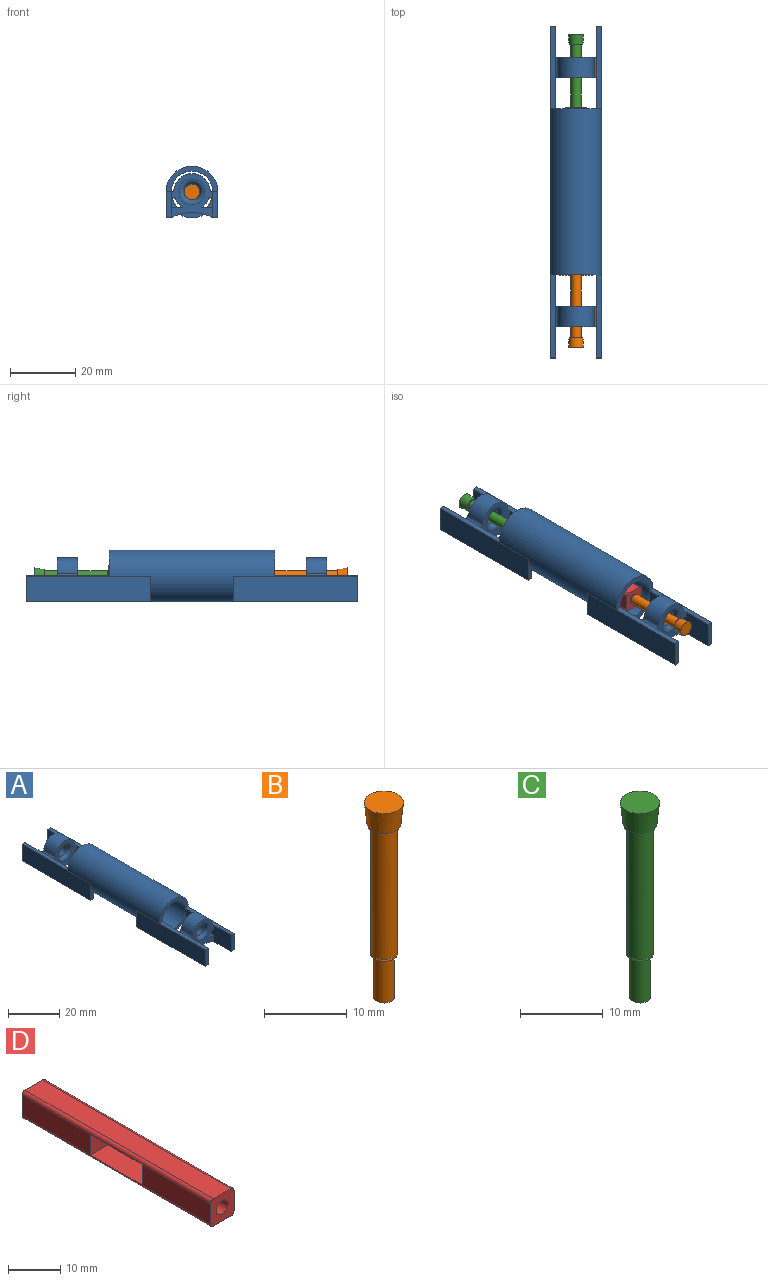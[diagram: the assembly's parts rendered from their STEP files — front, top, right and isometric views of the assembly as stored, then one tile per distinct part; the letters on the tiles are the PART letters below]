
ASSEMBLY  parts=4 mates=3
PART A: 68 faces, bbox 15.9x101.6x15.9 mm
  f0: cylinder r=6.35mm len=9.53mm, axis (0,1,0), area 1.3mm2, adj f2,f30,f31,f50
  f1: cylinder r=6.35mm len=69.85mm, axis (0,1,0), area 2031.9mm2, adj f2,f3,f4,f5,f8,f9,f10,f11
  f2: plane 38.1x7.87mm, normal (1,0,0), area 210.4mm2, adj f0,f1,f9,f15,f16,f22,f31,f45
  f3: plane 38.1x7.87mm, normal (-1,0,0), area 210.4mm2, adj f1,f7,f9,f12,f16,f24,f33,f47
  f4: plane 38.1x7.87mm, normal (1,0,0), area 210.4mm2, adj f1,f11,f16,f20,f21,f23,f27,f39
  f5: plane 38.1x7.87mm, normal (-1,0,0), area 210.4mm2, adj f1,f6,f11,f16,f17,f25,f29,f35
  f6: cylinder r=6.35mm len=9.53mm, axis (0,1,0), area 1.3mm2, adj f5,f28,f29,f41
  f7: cylinder r=6.35mm len=9.53mm, axis (0,1,0), area 1.3mm2, adj f3,f32,f33,f50
  f8: plane 15.87x7.87mm, normal (0,1,0), area 35.4mm2, adj f1,f16,f30,f32
  f9: plane 12.7x7.87mm, normal (0,1,0), area 25.3mm2, adj f1,f2,f3,f16
  f10: plane 15.87x7.87mm, normal (0,-1,0), area 35.4mm2, adj f1,f16,f26,f28
  f11: plane 12.7x7.87mm, normal (0,-1,0), area 25.3mm2, adj f1,f4,f5,f16
  f12: plane 38.1x1.59mm, normal (0,0,-1), area 60.5mm2, adj f3,f13,f24,f33,f53
  f13: plane 38.1x8mm, normal (1,0,0), area 303.3mm2, adj f12,f16,f24,f32,f33
  f14: plane 38.1x7.87mm, normal (-1,0,0), area 299.9mm2, adj f15,f16,f22,f31
  f15: plane 38.1x1.59mm, normal (0,0,-1), area 60.5mm2, adj f2,f14,f22,f31,f52
  f16: cylinder r=7.94mm len=101.6mm, axis (0,1,0), area 2284.2mm2, adj f2,f3,f4,f5,f8,f9,f10,f11
  f17: plane 38.1x1.59mm, normal (0,0,-1), area 60.5mm2, adj f5,f18,f25,f29,f54
  f18: plane 38.1x8mm, normal (1,0,0), area 303.3mm2, adj f16,f17,f25,f28,f29
  f19: plane 38.1x7.87mm, normal (-1,0,0), area 299.9mm2, adj f16,f20,f23,f27
  f20: plane 38.1x1.59mm, normal (0,0,-1), area 60.5mm2, adj f4,f19,f23,f27,f55
  f21: cylinder r=6.35mm len=9.53mm, axis (0,1,0), area 1.3mm2, adj f4,f26,f27,f41
  f22: plane 7.87x1.59mm, normal (0,-1,0), area 7.4mm2, adj f2,f14,f15,f16
  f23: plane 7.87x1.59mm, normal (0,1,0), area 7.4mm2, adj f4,f16,f19,f20
  f24: plane 7.87x1.59mm, normal (0,-1,0), area 7.4mm2, adj f3,f12,f13,f16
  f25: plane 7.87x1.59mm, normal (0,1,0), area 7.4mm2, adj f5,f16,f17,f18
  f26: plane 25.4x1.67mm, normal (0,0,1), area 40.8mm2, adj f1,f10,f16,f21,f27,f41,f42,f67
  f27: plane 8x1.59mm, normal (0,-1,0), area 12.7mm2, adj f4,f16,f19,f20,f21,f26
  f28: plane 25.4x1.67mm, normal (0,0,1), area 40.8mm2, adj f1,f6,f10,f18,f29,f41,f42,f66
  f29: plane 8x1.59mm, normal (0,-1,0), area 12.7mm2, adj f5,f6,f17,f18,f28
  f30: plane 25.4x1.67mm, normal (0,0,1), area 40.8mm2, adj f0,f1,f8,f16,f31,f50,f51,f65
  f31: plane 8x1.59mm, normal (0,1,0), area 12.7mm2, adj f0,f2,f14,f15,f16,f30
  f32: plane 25.4x1.67mm, normal (0,0,1), area 40.8mm2, adj f1,f7,f8,f13,f33,f50,f51,f64
  f33: plane 8x1.59mm, normal (0,1,0), area 12.7mm2, adj f3,f7,f12,f13,f32
  f34: plane 6.35x0.16mm, normal (0,0,-1), area 1mm2, adj f41,f42,f54,f55
  f35: plane 6.35x3.49mm, normal (0,0,1), area 22.1mm2, adj f5,f36,f41,f42
  f36: cylinder r=5.56mm len=6.35mm, axis (0,1,0), area 20.1mm2, adj f35,f41,f42,f62
  f37: cylinder r=5.56mm len=11.03mm, axis (0,1,0), area 102.3mm2, adj f41,f42,f66,f67
  f38: cylinder r=5.56mm len=6.35mm, axis (0,1,0), area 20.1mm2, adj f39,f41,f42,f63
  f39: plane 6.35x3.49mm, normal (0,0,1), area 22.1mm2, adj f4,f38,f41,f42
  f40: cylinder r=2.38mm len=4.76mm, axis (0,1,0), area 47.5mm2, adj f58,f59
  f41: plane 13.56x12.7mm, normal (0,-1,0), area 74.7mm2, adj f4,f5,f6,f21,f26,f28,f34,f35
  f42: plane 13.56x12.7mm, normal (0,1,0), area 74.7mm2, adj f1,f4,f5,f26,f28,f34,f35,f36
  f43: cylinder r=5.56mm len=11.03mm, axis (0,-1,0), area 102.3mm2, adj f50,f51,f64,f65
  f44: cylinder r=5.56mm len=6.35mm, axis (0,-1,0), area 20.1mm2, adj f45,f50,f51,f61
  f45: plane 6.35x3.49mm, normal (0,0,1), area 22.1mm2, adj f2,f44,f50,f51
  f46: plane 6.35x0.16mm, normal (0,0,-1), area 1mm2, adj f50,f51,f52,f53
  f47: plane 6.35x3.49mm, normal (0,0,1), area 22.1mm2, adj f3,f48,f50,f51
  f48: cylinder r=5.56mm len=6.35mm, axis (0,-1,0), area 20.1mm2, adj f47,f50,f51,f60
  f49: cylinder r=2.38mm len=4.76mm, axis (0,-1,0), area 47.5mm2, adj f56,f57
  f50: plane 13.56x12.7mm, normal (0,1,0), area 74.7mm2, adj f0,f2,f3,f7,f30,f32,f43,f44
  f51: plane 13.56x12.7mm, normal (0,-1,0), area 74.7mm2, adj f1,f2,f3,f30,f32,f43,f44,f45
  f52: cylinder r=12.7mm len=6.35mm, axis (0,-1,0), area 41.6mm2, adj f15,f46,f50,f51
  f53: cylinder r=12.7mm len=6.35mm, axis (0,1,0), area 41.6mm2, adj f12,f46,f50,f51
  f54: cylinder r=12.7mm len=6.35mm, axis (0,1,0), area 41.6mm2, adj f17,f34,f41,f42
  f55: cylinder r=12.7mm len=6.35mm, axis (0,-1,0), area 41.6mm2, adj f20,f34,f41,f42
  f56: torus R=3.97mm, axis (0,-1,0), area 46.3mm2, adj f49,f51
  f57: torus R=3.97mm, axis (0,-1,0), area 46.3mm2, adj f49,f50
  f58: torus R=3.97mm, axis (0,-1,0), area 46.3mm2, adj f40,f42
  f59: torus R=3.97mm, axis (0,-1,0), area 46.3mm2, adj f40,f41
  f60: cylinder r=1.59mm len=6.35mm, axis (0,1,0), area 10.9mm2, adj f3,f48,f50,f51
  f61: cylinder r=1.59mm len=6.35mm, axis (0,1,0), area 10.9mm2, adj f2,f44,f50,f51
  f62: cylinder r=1.59mm len=6.35mm, axis (0,-1,0), area 10.9mm2, adj f5,f36,f41,f42
  f63: cylinder r=1.59mm len=6.35mm, axis (0,-1,0), area 10.9mm2, adj f4,f38,f41,f42
  f64: cylinder r=0.76mm len=6.35mm, axis (0,-1,0), area 7mm2, adj f32,f43,f50,f51
  f65: cylinder r=0.76mm len=6.35mm, axis (0,-1,0), area 7mm2, adj f30,f43,f50,f51
  f66: cylinder r=0.76mm len=6.35mm, axis (0,1,0), area 7mm2, adj f28,f37,f41,f42
  f67: cylinder r=0.76mm len=6.35mm, axis (0,1,0), area 7mm2, adj f26,f37,f41,f42
PART B: 8 faces, bbox 4.8x4.8x28.9 mm
  f0: cylinder r=1.27mm len=6.35mm, axis (0,0,-1), area 50.7mm2, adj f1,f2
  f1: plane 2.54x2.54mm, normal (0,0,-1), area 5.1mm2, adj f0
  f2: plane 2.98x2.98mm, normal (0,0,-1), area 1.9mm2, adj f0,f3
  f3: torus R=1.49mm, axis (0,0,1), area 4mm2, adj f2,f4
  f4: cylinder r=1.59mm len=19.08mm, axis (0,0,-1), area 190.3mm2, adj f3,f6
  f5: plane 4.76x4.76mm, normal (0,0,1), area 17.8mm2, adj f7
  f6: plane 4.13x4.13mm, normal (0,0,-1), area 5.5mm2, adj f4,f7
  f7: cone r=2.38mm half-angle=5.7deg, axis (0,0,1), area 44.6mm2, adj f5,f6
PART C: 8 faces, bbox 4.8x4.8x28.9 mm
  f0: cylinder r=1.27mm len=6.35mm, axis (0,0,-1), area 50.7mm2, adj f1,f2
  f1: plane 2.54x2.54mm, normal (0,0,-1), area 5.1mm2, adj f0
  f2: plane 2.98x2.98mm, normal (0,0,-1), area 1.9mm2, adj f0,f3
  f3: torus R=1.49mm, axis (0,0,1), area 4mm2, adj f2,f4
  f4: cylinder r=1.59mm len=19.08mm, axis (0,0,-1), area 190.3mm2, adj f3,f6
  f5: plane 4.76x4.76mm, normal (0,0,1), area 17.8mm2, adj f7
  f6: plane 4.13x4.13mm, normal (0,0,-1), area 5.5mm2, adj f4,f7
  f7: cone r=2.38mm half-angle=5.7deg, axis (0,0,1), area 44.6mm2, adj f5,f6
PART D: 20 faces, bbox 6.4x50.8x6.4 mm
  f0: plane 18.42x4.76mm, normal (-1,0,0), area 87.7mm2, adj f6,f12,f17,f18
  f1: plane 18.42x4.76mm, normal (1,0,0), area 87.7mm2, adj f7,f14,f16,f19
  f2: plane 18.42x4.76mm, normal (1,0,0), area 87.7mm2, adj f6,f12,f16,f19
  f3: plane 50.8x4.76mm, normal (0,0,1), area 241.9mm2, adj f6,f7,f16,f17
  f4: plane 18.42x4.76mm, normal (-1,0,0), area 87.7mm2, adj f7,f14,f17,f18
  f5: plane 50.8x4.76mm, normal (0,0,-1), area 241.9mm2, adj f6,f7,f18,f19
  f6: plane 6.35x6.35mm, normal (0,-1,0), area 31.9mm2, adj f0,f2,f3,f5,f8,f16,f17,f18
  f7: plane 6.35x6.35mm, normal (0,1,0), area 31.9mm2, adj f1,f3,f4,f5,f10,f16,f17,f18
  f8: cylinder r=1.59mm len=6.35mm, axis (0,-1,0), area 63.3mm2, adj f6,f9
  f9: plane 3.18x3.18mm, normal (0,-1,0), area 7.9mm2, adj f8
  f10: cylinder r=1.59mm len=6.35mm, axis (0,1,0), area 63.3mm2, adj f7,f11
  f11: plane 3.18x3.18mm, normal (0,1,0), area 7.9mm2, adj f10
  f12: plane 6.35x4.76mm, normal (0,1,0), area 30.2mm2, adj f0,f2,f13,f15
  f13: plane 13.97x6.35mm, normal (0,0,-1), area 88.7mm2, adj f12,f14,f16,f17
  f14: plane 6.35x4.76mm, normal (0,-1,0), area 30.2mm2, adj f1,f4,f13,f15
  f15: plane 13.97x6.35mm, normal (0,0,1), area 88.7mm2, adj f12,f14,f18,f19
  f16: cylinder r=0.79mm len=50.8mm, axis (0,1,0), area 63.3mm2, adj f1,f2,f3,f6,f7,f13
  f17: cylinder r=0.79mm len=50.8mm, axis (0,-1,0), area 63.3mm2, adj f0,f3,f4,f6,f7,f13
  f18: cylinder r=0.79mm len=50.8mm, axis (0,1,0), area 63.3mm2, adj f0,f4,f5,f6,f7,f15
  f19: cylinder r=0.79mm len=50.8mm, axis (0,-1,0), area 63.3mm2, adj f1,f2,f5,f6,f7,f15
PLACE A t=(0,-0.3,0)mm
PLACE B rot(axis=(1,0,0),90deg) t=(-22.15,-19.05,31.36)mm
PLACE C rot(axis=(-1,0,0),90deg) t=(-28.5,19.05,-31.68)mm
PLACE D at identity
MATE revolute B.f0 <-> A.f36  axis (0,1,0) through (0,-35.23,0)mm
MATE fastened B.f0 <-> D.f8  axis (0,1,0) through (0,-19.05,0)mm
MATE fastened C.f0 <-> D.f8  axis (0,-1,0) through (0,19.05,0)mm
